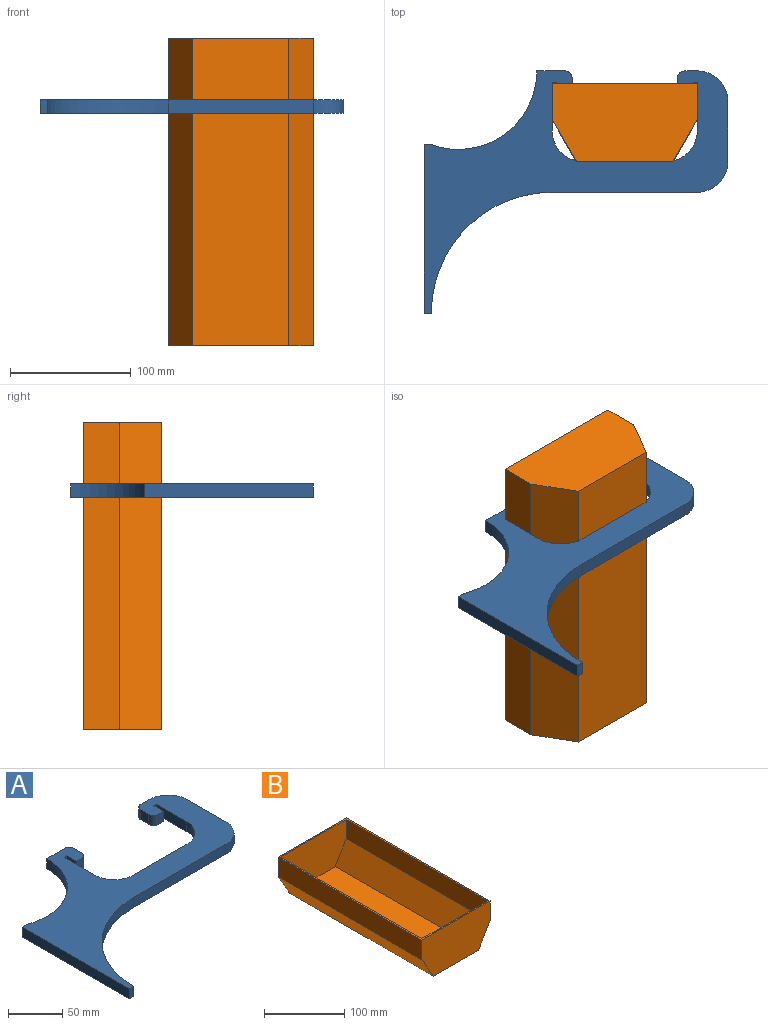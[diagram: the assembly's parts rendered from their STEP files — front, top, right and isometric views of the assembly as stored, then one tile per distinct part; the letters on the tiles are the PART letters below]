
ASSEMBLY  parts=2 mates=1
PART A: 30 faces, bbox 251.4x200.4x11.2 mm
  f0: plane 11.2x10mm, normal (1,0,0), area 112mm2, adj f1,f27,f28,f29
  f1: cylinder r=6.35mm len=11.2mm, axis (0,0,-1), area 111.7mm2, adj f0,f2,f28,f29
  f2: plane 22.85x11.2mm, normal (0,1,0), area 255.9mm2, adj f1,f3,f28,f29
  f3: cylinder r=65mm len=87.3mm, axis (0,0,-1), area 1398.5mm2, adj f2,f4,f28,f29
  f4: plane 11.2x6mm, normal (0,1,0), area 67.2mm2, adj f3,f5,f28,f29
  f5: plane 139.35x11.2mm, normal (-1,0,0), area 1560.7mm2, adj f4,f6,f28,f29
  f6: plane 11.2x6mm, normal (0,-1,0), area 67.2mm2, adj f5,f7,f28,f29
  f7: cylinder r=100mm len=100mm, axis (0,0,-1), area 1759.3mm2, adj f6,f8,f28,f29
  f8: plane 120x11.2mm, normal (0,-1,0), area 1344mm2, adj f7,f9,f28,f29
  f9: cylinder r=25.4mm len=25.4mm, axis (0,0,-1), area 446.9mm2, adj f8,f10,f28,f29
  f10: plane 49.6x11.2mm, normal (1,0,0), area 555.5mm2, adj f9,f11,f28,f29
  f11: cylinder r=25.4mm len=25.4mm, axis (0,0,-1), area 446.9mm2, adj f10,f12,f28,f29
  f12: plane 11.2x10.15mm, normal (0,1,0), area 113.7mm2, adj f11,f13,f28,f29
  f13: cylinder r=6.35mm len=11.2mm, axis (0,0,-1), area 111.7mm2, adj f12,f14,f28,f29
  f14: plane 11.2x10mm, normal (-1,0,0), area 112mm2, adj f13,f15,f28,f29
  f15: cylinder r=6.35mm len=11.2mm, axis (0,0,-1), area 111.7mm2, adj f14,f16,f28,f29
  f16: plane 11.2x6.65mm, normal (0,-1,0), area 74.5mm2, adj f15,f17,f28,f29
  f17: plane 12.7x11.2mm, normal (1,0,0), area 142.2mm2, adj f16,f18,f28,f29
  f18: plane 11.2x3.5mm, normal (0,-1,0), area 39.2mm2, adj f17,f19,f28,f29
  f19: plane 39.6x11.2mm, normal (-1,0,0), area 443.5mm2, adj f18,f20,f28,f29
  f20: cylinder r=25.4mm len=25.4mm, axis (0,0,-1), area 446.9mm2, adj f19,f21,f28,f29
  f21: plane 69.2x11.2mm, normal (0,1,0), area 775mm2, adj f20,f22,f28,f29
  f22: cylinder r=25.4mm len=25.4mm, axis (0,0,-1), area 446.9mm2, adj f21,f23,f28,f29
  f23: plane 39.6x11.2mm, normal (1,0,0), area 443.5mm2, adj f22,f24,f28,f29
  f24: plane 11.2x3.5mm, normal (0,-1,0), area 39.2mm2, adj f23,f25,f28,f29
  f25: plane 12.7x11.2mm, normal (-1,0,0), area 142.2mm2, adj f24,f26,f28,f29
  f26: plane 11.2x6.65mm, normal (0,-1,0), area 74.5mm2, adj f25,f27,f28,f29
  f27: cylinder r=6.35mm len=11.2mm, axis (0,0,-1), area 111.7mm2, adj f0,f26,f28,f29
  f28: plane 251.4x200.4mm, normal (0,0,1), area 14507mm2, adj f0,f1,f2,f3,f4,f5,f6,f7
  f29: plane 251.4x200.4mm, normal (0,0,-1), area 14507mm2, adj f0,f1,f2,f3,f4,f5,f6,f7
PART B: 15 faces, bbox 120x254x65 mm
  f0: plane 254x120mm, normal (0,0,1), area 1874.1mm2, adj f3,f4,f6,f7,f10,f11,f13,f14
  f1: plane 254x79.59mm, normal (0,0,-1), area 20214.7mm2, adj f2,f5,f6,f7
  f2: plane 254x35mm, normal (0.87,0,-0.5), area 10265.3mm2, adj f1,f3,f6,f7
  f3: plane 254x30mm, normal (1,0,0), area 7620mm2, adj f0,f2,f6,f7
  f4: plane 254x30mm, normal (-1,0,0), area 7620mm2, adj f0,f5,f6,f7
  f5: plane 254x35mm, normal (-0.87,0,-0.5), area 10265.3mm2, adj f1,f4,f6,f7
  f6: plane 120x65mm, normal (0,-1,0), area 7092.7mm2, adj f0,f1,f2,f3,f4,f5
  f7: plane 120x65mm, normal (0,1,0), area 7092.7mm2, adj f0,f1,f2,f3,f4,f5
  f8: plane 248.92x76.65mm, normal (0,0,1), area 19080.4mm2, adj f9,f12,f13,f14
  f9: plane 248.92x33.14mm, normal (-0.87,0,0.5), area 9525.5mm2, adj f8,f10,f13,f14
  f10: plane 248.92x29.32mm, normal (-1,0,0), area 7298.2mm2, adj f0,f9,f13,f14
  f11: plane 248.92x29.32mm, normal (1,0,0), area 7298.2mm2, adj f0,f12,f13,f14
  f12: plane 248.92x33.14mm, normal (0.87,0,0.5), area 9525.5mm2, adj f8,f11,f13,f14
  f13: plane 114.92x62.46mm, normal (0,1,0), area 6543.8mm2, adj f0,f8,f9,f10,f11,f12
  f14: plane 114.92x62.46mm, normal (0,-1,0), area 6543.8mm2, adj f0,f8,f9,f10,f11,f12
PLACE A t=(-24.15,-106.12,13.43)mm
PLACE B rot(axis=(-1,0,0),90deg) t=(35.85,19.05,-178.57)mm
MATE fastened B.f4 <-> A.f23  axis (-1,0,0) through (-24.15,84.05,75.43)mm
